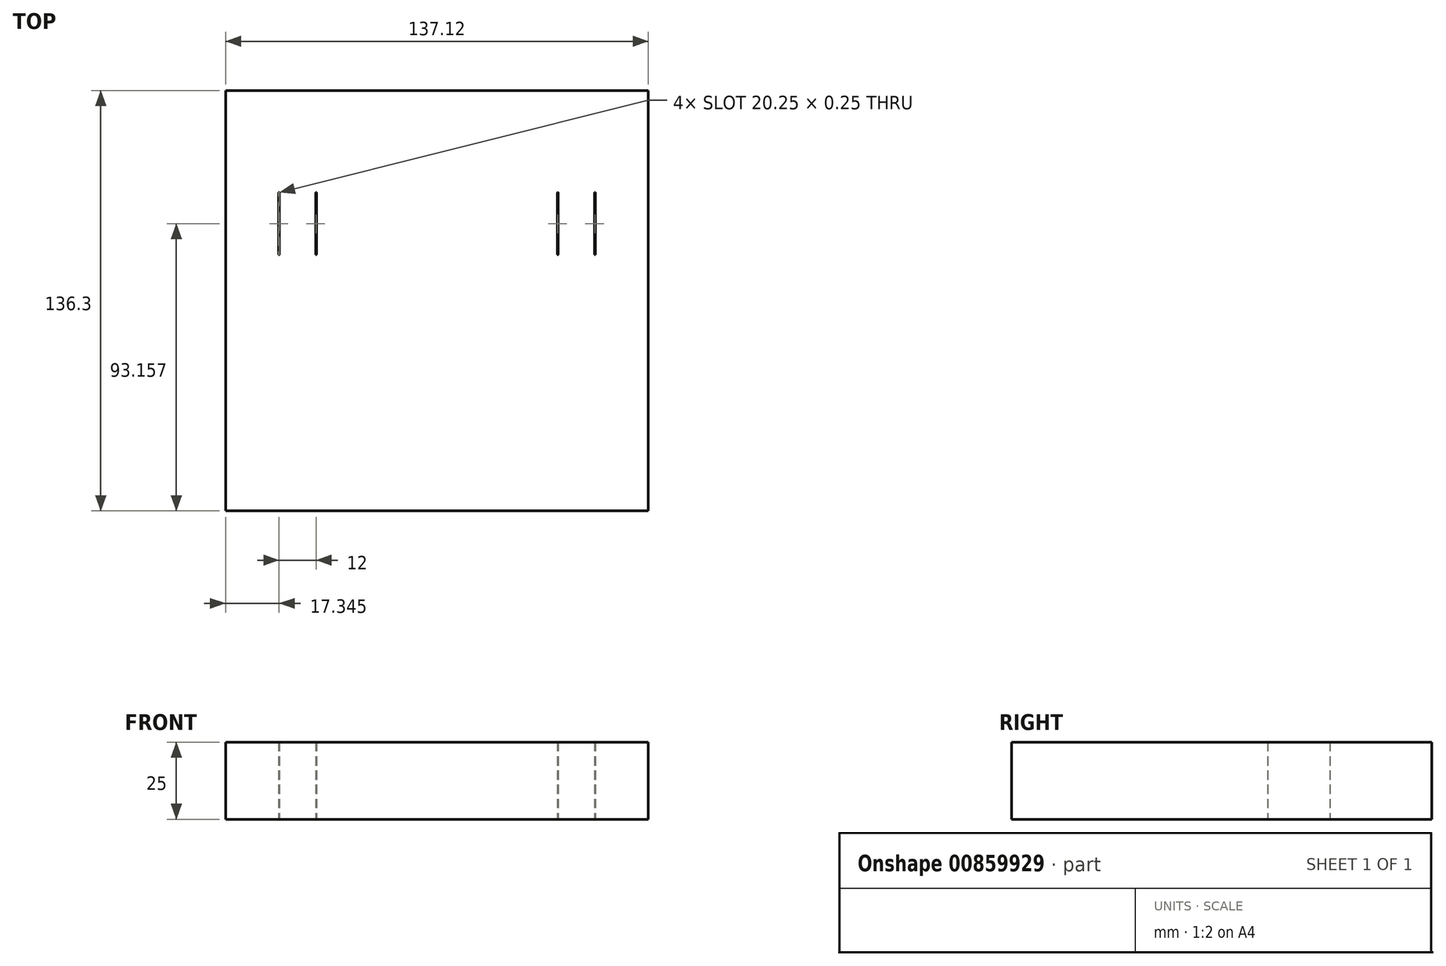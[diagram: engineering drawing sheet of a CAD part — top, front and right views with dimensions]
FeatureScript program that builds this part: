
annotation { "Feature Type Name" : "Feature", "Feature Type Description" : "" }
export const myFeature = defineFeature(function(context is Context, id is Id, definition is map)
    precondition{}
    {
        {
            var Q0;
            Q0=qCreatedBy(makeId("Top.planeOp"),FACE);
            var sketch = newSketch(context, id + "F0", { "sketchPlane" : qUnion([Q0])});
            skLineSegment(sketch, "E0.bottom", {"start": v(-68.56, 68.15) * mm, "end": v(68.56, 68.15) * mm});
            skLineSegment(sketch, "E0.top", {"start": v(-68.56, -68.15) * mm, "end": v(68.56, -68.15) * mm});
            skLineSegment(sketch, "E0.left", {"start": v(-68.56, 68.15) * mm, "end": v(-68.56, -68.15) * mm});
            skLineSegment(sketch, "E0.right", {"start": v(68.56, 68.15) * mm, "end": v(68.56, -68.15) * mm});
            skPoint(sketch, "E0.middle", {"position": v(0, 0) * mm});
            skLineSegment(sketch, "E1", {"start": v(-51.22, 35) * mm, "end": v(-51.22, 15) * mm});
            skLineSegment(sketch, "E2", {"start": v(-39.22, 35) * mm, "end": v(-39.22, 15) * mm});
            skArc(sketch, "E3.0.startCap", {"start": v(-39.34, 35) * mm, "mid": v(-39.22, 35.13) * mm, "end": v(-39.1, 35) * mm});
            skArc(sketch, "E3.0.endCap", {"start": v(-39.1, 15) * mm, "mid": v(-39.22, 14.88) * mm, "end": v(-39.34, 15) * mm});
            skLineSegment(sketch, "E3.0.left", {"start": v(-39.1, 35) * mm, "end": v(-39.1, 15) * mm});
            skLineSegment(sketch, "E3.0.right", {"start": v(-39.34, 35) * mm, "end": v(-39.34, 15) * mm});
            skArc(sketch, "E3.1.startCap", {"start": v(-51.34, 35) * mm, "mid": v(-51.22, 35.13) * mm, "end": v(-51.1, 35) * mm});
            skArc(sketch, "E3.1.endCap", {"start": v(-51.1, 15) * mm, "mid": v(-51.22, 14.88) * mm, "end": v(-51.34, 15) * mm});
            skLineSegment(sketch, "E3.1.left", {"start": v(-51.1, 35) * mm, "end": v(-51.1, 15) * mm});
            skLineSegment(sketch, "E3.1.right", {"start": v(-51.34, 35) * mm, "end": v(-51.34, 15) * mm});
            skArc(sketch, "E4.MirrorCS", {"start": v(39.34, 35) * mm, "mid": v(39.22, 35.13) * mm, "end": v(39.1, 35) * mm});
            skArc(sketch, "E5.MirrorCS", {"start": v(51.1, 15) * mm, "mid": v(51.22, 14.88) * mm, "end": v(51.34, 15) * mm});
            skArc(sketch, "E6.MirrorCS", {"start": v(51.34, 35) * mm, "mid": v(51.22, 35.13) * mm, "end": v(51.1, 35) * mm});
            skArc(sketch, "E7.MirrorCS", {"start": v(39.1, 15) * mm, "mid": v(39.22, 14.88) * mm, "end": v(39.34, 15) * mm});
            skLineSegment(sketch, "E8.MirrorCS", {"start": v(39.1, 35) * mm, "end": v(39.1, 15) * mm});
            skLineSegment(sketch, "E9.MirrorCS", {"start": v(51.34, 35) * mm, "end": v(51.34, 15) * mm});
            skLineSegment(sketch, "E10.MirrorCS", {"start": v(51.22, 35) * mm, "end": v(51.22, 15) * mm});
            skLineSegment(sketch, "E11.MirrorCS", {"start": v(39.34, 35) * mm, "end": v(39.34, 15) * mm});
            skLineSegment(sketch, "E12.MirrorCS", {"start": v(39.22, 35) * mm, "end": v(39.22, 15) * mm});
            skLineSegment(sketch, "E13.MirrorCS", {"start": v(51.1, 35) * mm, "end": v(51.1, 15) * mm});
            skSolve(sketch);
        }
        {
            var Q0;
            Q0 = qSketchRegion(id + "F0", true);
            extrude(context, id + "F1", {"entities" : qUnion([Q0]), "depth" : 25 * mm, "offsetDistance" : 25 * mm});
        }
    });
